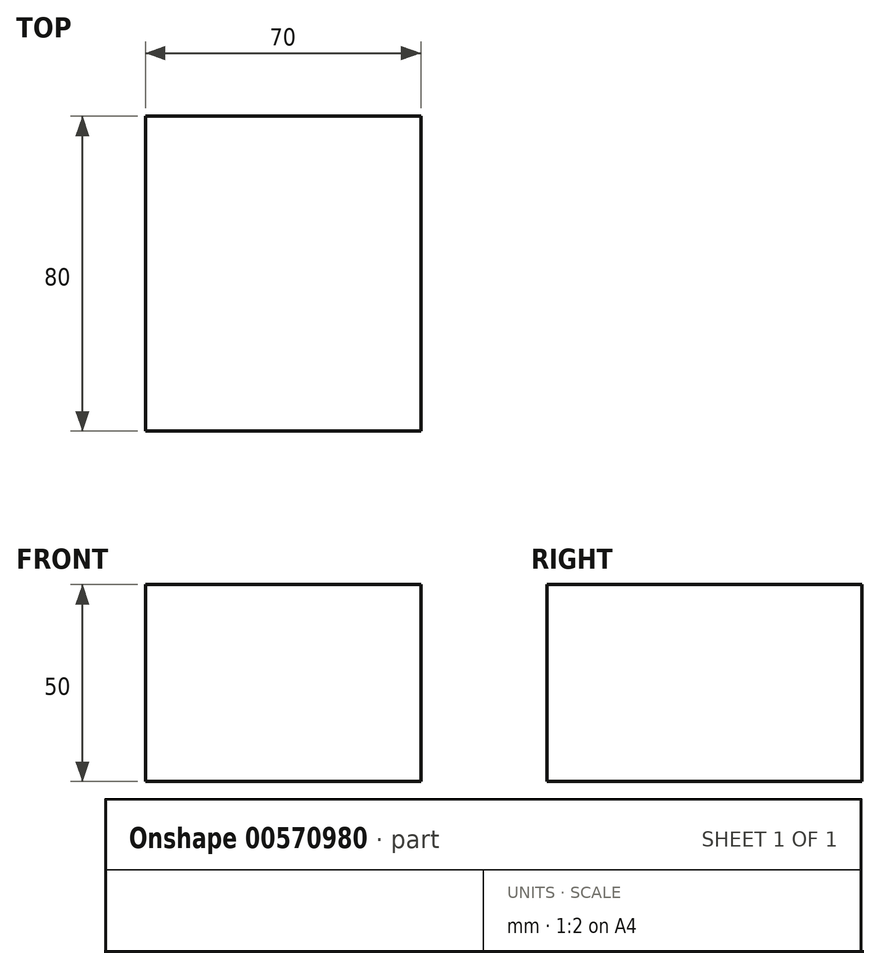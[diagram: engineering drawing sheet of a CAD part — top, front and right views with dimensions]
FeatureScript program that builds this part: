
annotation { "Feature Type Name" : "Feature", "Feature Type Description" : "" }
export const myFeature = defineFeature(function(context is Context, id is Id, definition is map)
    precondition{}
    {
        {
            var Q0;
            Q0=qCreatedBy(makeId("Top.planeOp"),FACE);
            var sketch = newSketch(context, id + "F0", { "sketchPlane" : qUnion([Q0])});
            skLineSegment(sketch, "E0.bottom", {"start": v(-34, 45.29) * mm, "end": v(36, 45.29) * mm});
            skLineSegment(sketch, "E0.top", {"start": v(-34, -34.71) * mm, "end": v(36, -34.71) * mm});
            skLineSegment(sketch, "E0.left", {"start": v(-34, 45.29) * mm, "end": v(-34, -34.71) * mm});
            skLineSegment(sketch, "E0.right", {"start": v(36, 45.29) * mm, "end": v(36, -34.71) * mm});
            skSolve(sketch);
        }
        {
            var Q0;
            Q0 = qSketchRegion(id + "F0", true);
            extrude(context, id + "F1", {"entities" : qUnion([Q0]), "depth" : 50 * mm, "offsetDistance" : 25 * mm});
        }
    });
